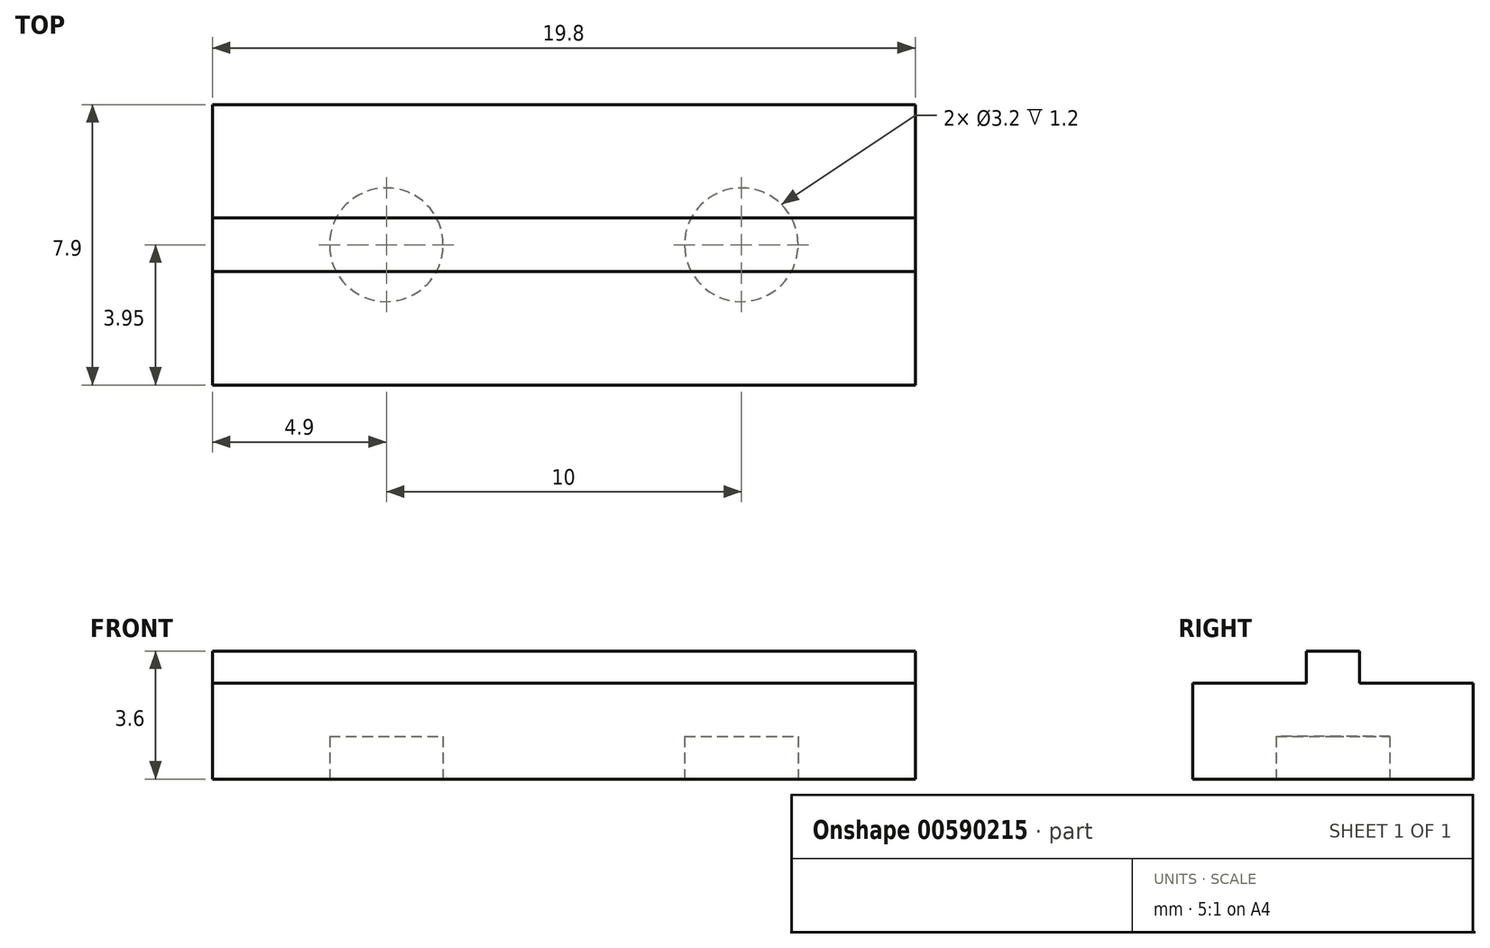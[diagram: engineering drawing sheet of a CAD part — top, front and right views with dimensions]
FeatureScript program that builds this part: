
annotation { "Feature Type Name" : "Feature", "Feature Type Description" : "" }
export const myFeature = defineFeature(function(context is Context, id is Id, definition is map)
    precondition{}
    {
        {
            var Q0;
            Q0=qCreatedBy(makeId("Top.planeOp"),FACE);
            var sketch = newSketch(context, id + "F0", { "sketchPlane" : qUnion([Q0])});
            skPoint(sketch, "E0.middle", {"position": v(0, 0) * mm});
            skLineSegment(sketch, "E1.bottom", {"start": v(-9.9, 3.95) * mm, "end": v(9.9, 3.95) * mm});
            skLineSegment(sketch, "E1.top", {"start": v(-9.9, 0.75) * mm, "end": v(9.9, 0.75) * mm});
            skLineSegment(sketch, "E1.left", {"start": v(-9.9, 3.95) * mm, "end": v(-9.9, 0.75) * mm});
            skLineSegment(sketch, "E1.right", {"start": v(9.9, 3.95) * mm, "end": v(9.9, 0.75) * mm});
            skPoint(sketch, "E1.middle", {"position": v(0, 2.35) * mm});
            skLineSegment(sketch, "E2.bottom", {"start": v(-9.9, -0.75) * mm, "end": v(9.9, -0.75) * mm});
            skLineSegment(sketch, "E2.top", {"start": v(-9.9, -3.95) * mm, "end": v(9.9, -3.95) * mm});
            skLineSegment(sketch, "E2.left", {"start": v(-9.9, -0.75) * mm, "end": v(-9.9, -3.95) * mm});
            skLineSegment(sketch, "E2.right", {"start": v(9.9, -0.75) * mm, "end": v(9.9, -3.95) * mm});
            skPoint(sketch, "E2.middle", {"position": v(0, -2.35) * mm});
            skLineSegment(sketch, "E3.bottom", {"start": v(-12, 6) * mm, "end": v(12, 6) * mm});
            skLineSegment(sketch, "E3.top", {"start": v(-12, -6) * mm, "end": v(12, -6) * mm});
            skLineSegment(sketch, "E3.left", {"start": v(-12, 6) * mm, "end": v(-12, -6) * mm});
            skLineSegment(sketch, "E3.right", {"start": v(12, 6) * mm, "end": v(12, -6) * mm});
            skLineSegment(sketch, "E4", {"start": v(-9.9, 0.75) * mm, "end": v(-9.9, -0.75) * mm});
            skLineSegment(sketch, "E5", {"start": v(9.9, 0.75) * mm, "end": v(9.9, -0.75) * mm});
            skSolve(sketch);
        }
        {
            var Q0;
            Q0=makeQuery(id+"F0.imprint","IMPRINT",FACE,{"disambiguationData":[TD([[makeQuery(id+"F0.imprint","IMPRINT",EDGE,{"derivedFrom":sQuery(id+"F0.wireOp",EDGE,"E1.top")}),-1.0]])]});
            extrude(context, id + "F1", {"entities" : qUnion([Q0]), "depth" : .9 * mm, "offsetDistance" : 25 * mm});
        }
        {
            var Q0;
            Q0=makeQuery(id+"F1.opExtrude","CAP_FACE",FACE,{"disambiguationData":[OSD([sQuery(id+"F0.wireOp",EDGE,"E1.bottom"),sQuery(id+"F0.wireOp",EDGE,"E1.top"),sQuery(id+"F0.wireOp",EDGE,"E1.left"),sQuery(id+"F0.wireOp",EDGE,"E1.right"),sQuery(id+"F0.wireOp",EDGE,"E2.bottom"),sQuery(id+"F0.wireOp",EDGE,"E2.top"),sQuery(id+"F0.wireOp",EDGE,"E2.left"),sQuery(id+"F0.wireOp",EDGE,"E2.right"),sQuery(id+"F0.wireOp",EDGE,"E3.bottom"),sQuery(id+"F0.wireOp",EDGE,"E3.top"),sQuery(id+"F0.wireOp",EDGE,"E3.left"),sQuery(id+"F0.wireOp",EDGE,"E3.right")])],"isStart":true});
            var sketch = newSketch(context, id + "F2", { "sketchPlane" : qUnion([Q0])});
            skLineSegment(sketch, "E6.bottom", {"start": v(9.9, 3.95) * mm, "end": v(-9.9, 3.95) * mm});
            skLineSegment(sketch, "E6.top", {"start": v(9.9, -3.95) * mm, "end": v(-9.9, -3.95) * mm});
            skLineSegment(sketch, "E6.left", {"start": v(9.9, 3.95) * mm, "end": v(9.9, -3.95) * mm});
            skLineSegment(sketch, "E6.right", {"start": v(-9.9, 3.95) * mm, "end": v(-9.9, -3.95) * mm});
            skPoint(sketch, "E6.middle", {"position": v(0, 0) * mm});
            skSolve(sketch);
        }
        {
            var Q0;
            Q0=qSketchRegion(id+"F2",true);
            extrude(context, id + "F3", {"entities" : qUnion([Q0]), "operationType" : NewBodyOperationType.ADD, "depth" : 2.7 * mm, "offsetDistance" : 25 * mm});
        }
        {
            var Q0;
            Q0=makeQuery(id+"F3.opExtrude","CAP_FACE",FACE,{"disambiguationData":[OSD([sQuery(id+"F2.wireOp",EDGE,"E6.bottom"),sQuery(id+"F2.wireOp",EDGE,"E6.top"),sQuery(id+"F2.wireOp",EDGE,"E6.left"),sQuery(id+"F2.wireOp",EDGE,"E6.right")])],"isStart":false});
            var sketch = newSketch(context, id + "F4", { "sketchPlane" : qUnion([Q0])});
            skCircle(sketch, "E7", {"center": v(-5, 0) * mm, "radius": 1.6 * mm});
            skCircle(sketch, "E8", {"center": v(5, 0) * mm, "radius": 1.6 * mm});
            skSolve(sketch);
        }
        {
            var Q0;
            Q0=qSketchRegion(id+"F4",true);
            extrude(context, id + "F5", {"entities" : qUnion([Q0]), "operationType" : NewBodyOperationType.REMOVE, "oppositeDirection" : true, "depth" : 1.2 * mm, "offsetDistance" : 25 * mm});
        }
    });
